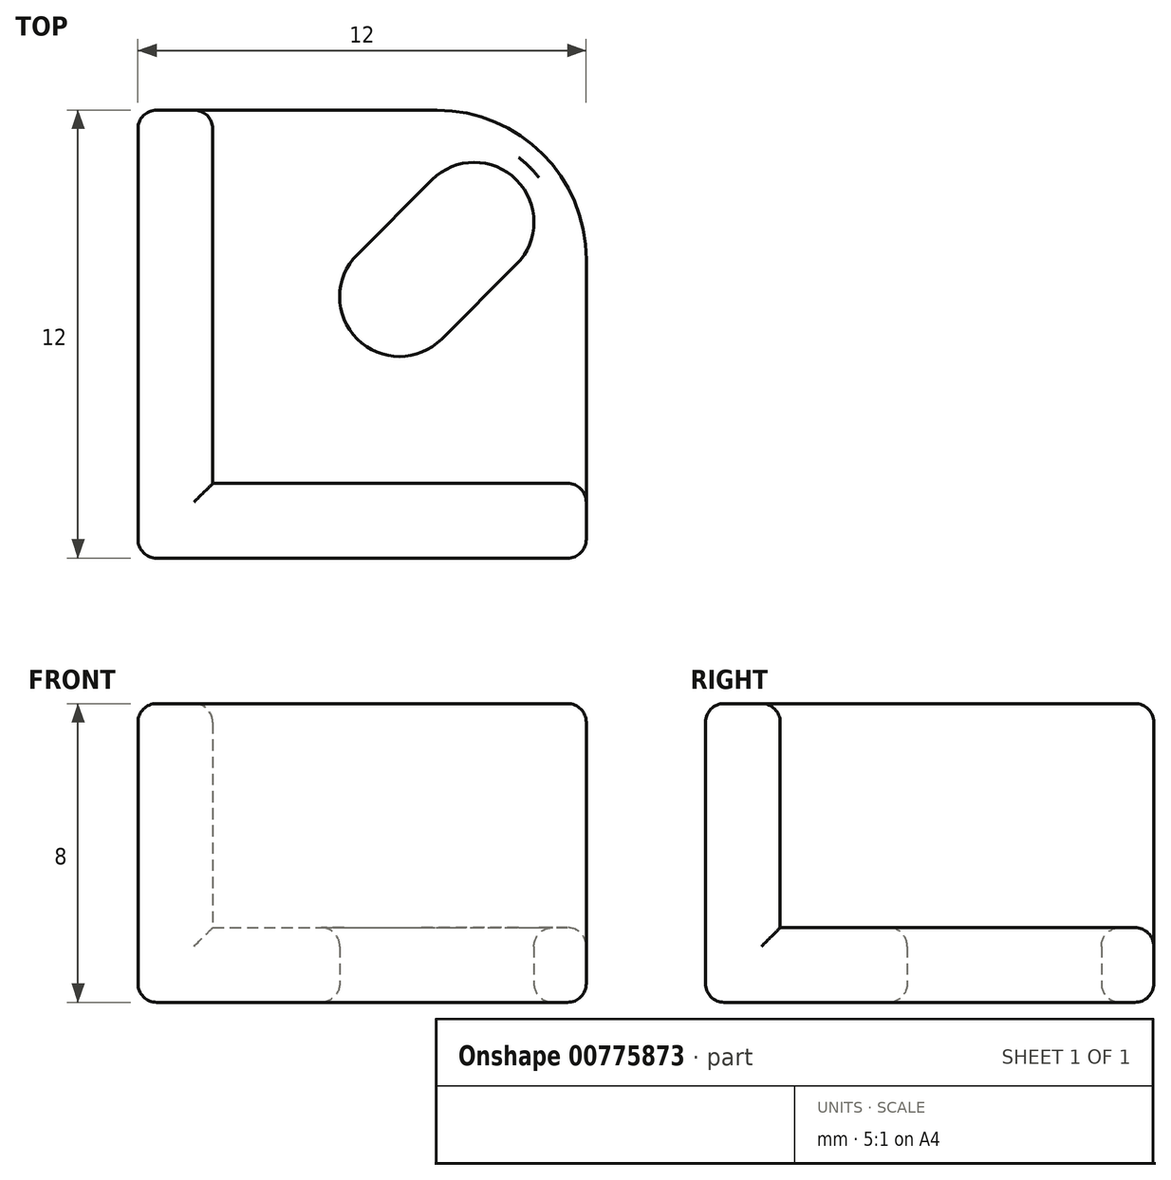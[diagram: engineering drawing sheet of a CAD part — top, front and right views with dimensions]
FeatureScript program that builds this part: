
annotation { "Feature Type Name" : "Feature", "Feature Type Description" : "" }
export const myFeature = defineFeature(function(context is Context, id is Id, definition is map)
    precondition{}
    {
        {
            var Q0;
            Q0=qCreatedBy(makeId("Top.planeOp"),FACE);
            var sketch = newSketch(context, id + "F0", { "sketchPlane" : qUnion([Q0])});
            skLineSegment(sketch, "E0.bottom", {"start": v(-12.43, 10.54) * mm, "end": v(-10.43, 10.54) * mm});
            skLineSegment(sketch, "E0.top", {"start": v(-12.43, -1.46) * mm, "end": v(-0.43, -1.46) * mm});
            skLineSegment(sketch, "E0.left", {"start": v(-12.43, 10.54) * mm, "end": v(-12.43, -1.46) * mm});
            skLineSegment(sketch, "E0.right", {"start": v(-0.43, 0.54) * mm, "end": v(-0.43, -1.46) * mm});
            skLineSegment(sketch, "E1", {"start": v(-10.43, 10.54) * mm, "end": v(-10.43, 0.54) * mm});
            skLineSegment(sketch, "E2", {"start": v(-10.43, 0.54) * mm, "end": v(-0.43, 0.54) * mm});
            skArc(sketch, "E3", {"start": v(-2.3, 6.4) * mm, "mid": v(-2.3, 8.67) * mm, "end": v(-4.56, 8.67) * mm});
            skLineSegment(sketch, "E4", {"start": v(-10.43, 10.54) * mm, "end": v(-0.43, 10.54) * mm});
            skLineSegment(sketch, "E5", {"start": v(-0.43, 10.54) * mm, "end": v(-0.43, 0.54) * mm});
            skArc(sketch, "E6", {"start": v(-6.56, 6.67) * mm, "mid": v(-6.56, 4.4) * mm, "end": v(-4.3, 4.4) * mm});
            skLineSegment(sketch, "E7", {"start": v(-6.56, 6.67) * mm, "end": v(-4.56, 8.67) * mm});
            skLineSegment(sketch, "E8", {"start": v(-4.3, 4.4) * mm, "end": v(-2.3, 6.4) * mm});
            skSolve(sketch);
        }
        {
            var Q0;
            Q0=makeQuery(id+"F0.imprint","IMPRINT",FACE,{"disambiguationData":[TD([[makeQuery(id+"F0.imprint","IMPRINT",EDGE,{"derivedFrom":sQuery(id+"F0.wireOp",EDGE,"E0.bottom")}),-1.0]])]});
            extrude(context, id + "F1", {"entities" : qUnion([Q0]), "depth" : 8 * mm, "offsetDistance" : 25 * mm});
        }
        {
            var Q0;
            Q0 = qSketchRegion(id + "F0", true);
            extrude(context, id + "F2", {"entities" : qUnion([Q0]), "operationType" : NewBodyOperationType.ADD, "depth" : 2 * mm, "offsetDistance" : 25 * mm});
        }
        {
            var Q0;
            Q0=makeQuery(id+"F2.opExtrude","SWEPT_EDGE",EDGE,{"disambiguationData":[OSD([sQuery(id+"F0.wireOp",EDGE,"E4"),sQuery(id+"F0.wireOp",EDGE,"E5")])]});
            fillet(context, id + "F3", {"entities" : qUnion([Q0]), "radius" : 4 * mm, "tangentPropagation" : true, "allowEdgeOverflow" : false});
        }
        {
            var Q0;
            {var subQ0=sQuery(id+"F0.wireOp",EDGE,"E0.right");Q0=makeQuery(id+"F2.boolean.opBoolean","MERGE",FACE,{"derivedFrom":[makeQuery(id+"F1.opExtrude","SWEPT_FACE",FACE,{"disambiguationData":[OSD([subQ0])]}),makeQuery(id+"F2.opExtrude","SWEPT_FACE",FACE,{"disambiguationData":[OSD([subQ0,sQuery(id+"F0.wireOp",EDGE,"E5")])]})]});}
            var Q1;
            Q1=makeQuery(id+"F3.opFillet","BLEND_FACE",FACE,{"disambiguationData":[OSD([sQuery(id+"F0.wireOp",EDGE,"E4"),sQuery(id+"F0.wireOp",EDGE,"E5")])]});
            var Q2;
            Q2=makeQuery(id+"F1.opExtrude","CAP_FACE",FACE,{"disambiguationData":[OSD([sQuery(id+"F0.wireOp",EDGE,"E0.bottom"),sQuery(id+"F0.wireOp",EDGE,"E0.top"),sQuery(id+"F0.wireOp",EDGE,"E0.left"),sQuery(id+"F0.wireOp",EDGE,"E0.right"),sQuery(id+"F0.wireOp",EDGE,"E1"),sQuery(id+"F0.wireOp",EDGE,"E2")])],"isStart":false});
            var Q3;
            Q3=makeQuery(id+"F1.opExtrude","SWEPT_FACE",FACE,{"disambiguationData":[OSD([sQuery(id+"F0.wireOp",EDGE,"E0.top")])]});
            var Q4;
            Q4=makeQuery(id+"F1.opExtrude","SWEPT_FACE",FACE,{"disambiguationData":[OSD([sQuery(id+"F0.wireOp",EDGE,"E0.left")])]});
            var Q5;
            Q5=makeQuery(id+"F2.opExtrude","CAP_EDGE",EDGE,{"disambiguationData":[OSD([sQuery(id+"F0.wireOp",EDGE,"E8")])],"isStart":true});
            var Q6;
            Q6=makeQuery(id+"F2.opExtrude","CAP_EDGE",EDGE,{"disambiguationData":[OSD([sQuery(id+"F0.wireOp",EDGE,"E6")])],"isStart":true});
            var Q7;
            Q7=makeQuery(id+"F2.opExtrude","CAP_EDGE",EDGE,{"disambiguationData":[OSD([sQuery(id+"F0.wireOp",EDGE,"E6")])],"isStart":false});
            var Q8;
            Q8=makeQuery(id+"F2.opExtrude","CAP_EDGE",EDGE,{"disambiguationData":[OSD([sQuery(id+"F0.wireOp",EDGE,"E7")])],"isStart":false});
            fillet(context, id + "F4", {"entities" : qUnion([Q0, Q1, Q2, Q3, Q4, Q5, Q6, Q7, Q8]), "radius" : .5 * mm, "tangentPropagation" : true, "allowEdgeOverflow" : false});
        }
        {
            var Q0;
            {var subQ0=sQuery(id+"F0.wireOp",EDGE,"E0.bottom");Q0=makeQuery(id+"F2.boolean.opBoolean","MERGE",FACE,{"derivedFrom":[makeQuery(id+"F1.opExtrude","SWEPT_FACE",FACE,{"disambiguationData":[OSD([subQ0])]}),makeQuery(id+"F2.opExtrude","SWEPT_FACE",FACE,{"disambiguationData":[OSD([subQ0,sQuery(id+"F0.wireOp",EDGE,"E4")])]})]});}
            fillet(context, id + "F5", {"entities" : qUnion([Q0]), "radius" : .5 * mm, "tangentPropagation" : true, "allowEdgeOverflow" : false});
        }
    });
